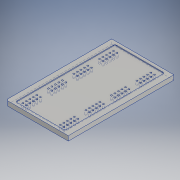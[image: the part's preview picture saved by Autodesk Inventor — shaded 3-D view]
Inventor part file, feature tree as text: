
AUTODESK INVENTOR PART (.ipt)
format: ipt  version: 2019.4 (Build 234330000, 330)  size: 229,888 bytes
history: native  units: in
note: dims shown in document units (in); Inventor stores cm internally (conversion verified against a paired STEP export)
features: sketch x3, extrude x2, hole x1, fillet x1, chamfer x1
ambient origin geometry x8: Origin, YZ Plane, XZ Plane, XY Plane, X Axis, Y Axis, Z Axis, Center Point
bodies: Solid1 (feature_tree)
feature tree (8):
  extrude  "Extrusion1"  Depth=8.5in
  extrude  "Extrusion7"  Depth=0.25in
  hole  "Hole2"  [1 undecoded]
  fillet  "Fillet1"  Radius=0.5in
  chamfer  "Chamfer1"  Distance=0.0625in
  sketch  "Sketch1"  dims[d0=5.0in d1=8.5in]
  sketch  "Sketch8"  dims[d2=0.375in d3=0.0in d91=0.25in]
  sketch  "Sketch9"  dims[d92=0.5in d93=0.25in d95=0.5in d96=0.0625in d97=0.0in d100=0.35in d101=0.25in d102=1.9685in d104=0.2812in d105=0.7874in d107=0.2812in d110=1.5748in d112=2.055in d113=0.7874in d115=3.0185in d118=0.125in d119=0.75in d120=0.375in d121=0.25in d122=0.5635in d123=1.0in d124=0.8108in d125=0.125in d126=0.125in d127=0.125in d128=45.0deg]
note: 1 required parameter value undecoded (feature->parameter linkage not recoverable at this tier; creation-order binding heuristic only, values carry confidence <= 0.55)
